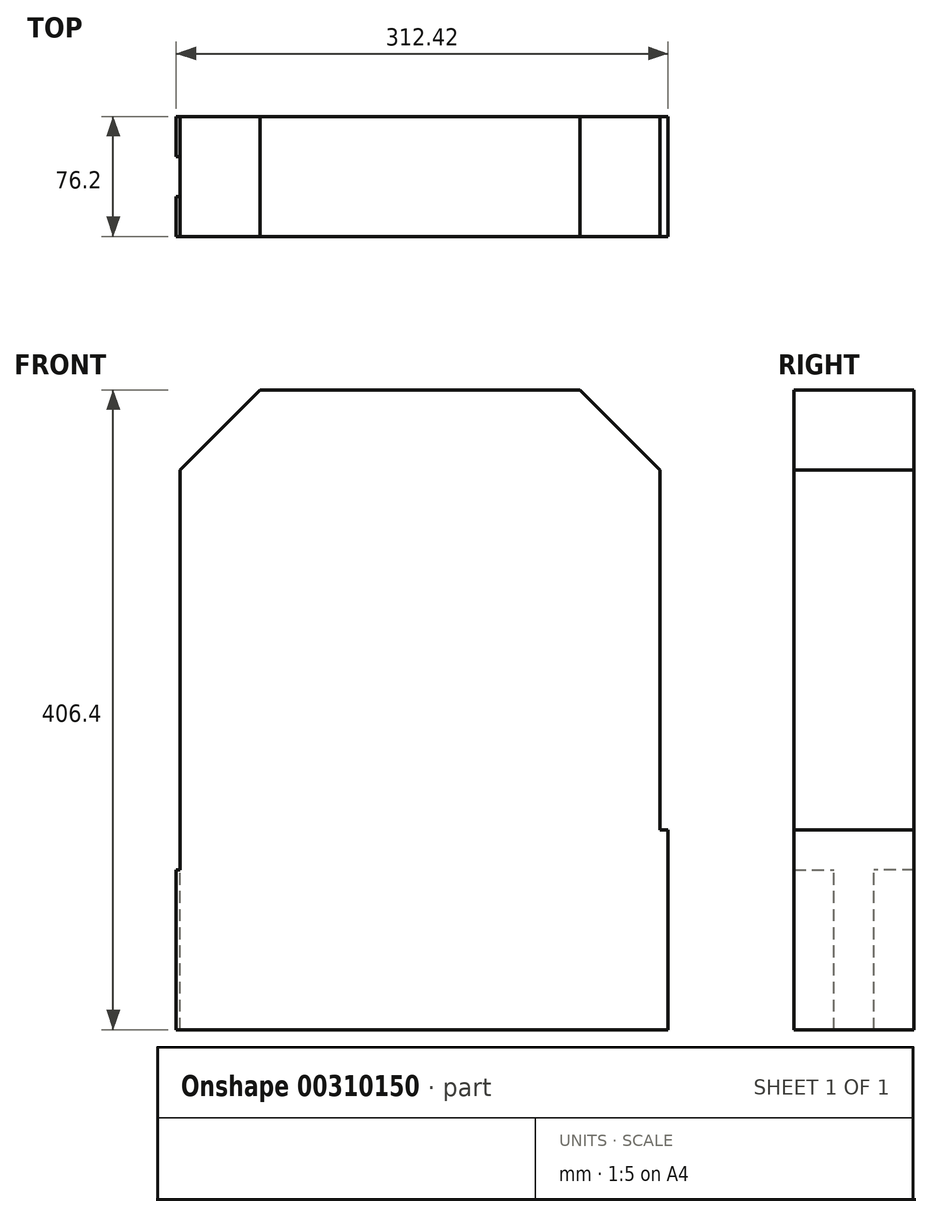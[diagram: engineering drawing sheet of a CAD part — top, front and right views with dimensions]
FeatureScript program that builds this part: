
annotation { "Feature Type Name" : "Feature", "Feature Type Description" : "" }
export const myFeature = defineFeature(function(context is Context, id is Id, definition is map)
    precondition{}
    {
        {
            var Q0;
            Q0=qCreatedBy(makeId("Front.planeOp"),FACE);
            var sketch = newSketch(context, id + "F0", { "sketchPlane" : qUnion([Q0])});
            skLineSegment(sketch, "E0.bottom", {"start": v(-152.4, 203.2) * mm, "end": v(152.4, 203.2) * mm});
            skLineSegment(sketch, "E0.top", {"start": v(-152.4, -203.2) * mm, "end": v(152.4, -203.2) * mm});
            skLineSegment(sketch, "E0.left", {"start": v(-152.4, 203.2) * mm, "end": v(-152.4, -203.2) * mm});
            skLineSegment(sketch, "E0.right", {"start": v(152.4, 203.2) * mm, "end": v(152.4, -203.2) * mm});
            skSolve(sketch);
        }
        {
            var Q0;
            Q0=makeQuery(id+"F0.imprint","IMPRINT",FACE,{"disambiguationData":[TD([[makeQuery(id+"F0.imprint","IMPRINT",EDGE,{"derivedFrom":sQuery(id+"F0.wireOp",EDGE,"E0.bottom")}),-1.0]])]});
            extrude(context, id + "F1", {"entities" : qUnion([Q0]), "depth" : 76.2 * mm});
        }
        {
            var Q0;
            Q0=makeQuery(id+"F1.opExtrude","SWEPT_EDGE",EDGE,{"disambiguationData":[OSD([sQuery(id+"F0.wireOp",EDGE,"E0.bottom"),sQuery(id+"F0.wireOp",EDGE,"E0.left")])]});
            var Q1;
            Q1=makeQuery(id+"F1.opExtrude","SWEPT_EDGE",EDGE,{"disambiguationData":[OSD([sQuery(id+"F0.wireOp",EDGE,"E0.bottom"),sQuery(id+"F0.wireOp",EDGE,"E0.right")])]});
            chamfer(context, id + "F2", {"entities" : qUnion([Q0, Q1]), "width" : 50.8 * mm, "tangentPropagation" : true});
        }
        {
            var Q0;
            Q0=makeQuery(id+"F1.opExtrude","SWEPT_FACE",FACE,{"disambiguationData":[OSD([sQuery(id+"F0.wireOp",EDGE,"E0.left")])]});
            var sketch = newSketch(context, id + "F3", { "sketchPlane" : qUnion([Q0])});
            skLineSegment(sketch, "E1.bottom", {"start": v(0, -203.2) * mm, "end": v(25.4, -203.2) * mm});
            skLineSegment(sketch, "E1.top", {"start": v(0, -101.6) * mm, "end": v(25.4, -101.6) * mm});
            skLineSegment(sketch, "E1.left", {"start": v(0, -203.2) * mm, "end": v(0, -101.6) * mm});
            skLineSegment(sketch, "E1.right", {"start": v(25.4, -203.2) * mm, "end": v(25.4, -101.6) * mm});
            skLineSegment(sketch, "E2.bottom", {"start": v(76.2, -203.2) * mm, "end": v(50.8, -203.2) * mm});
            skLineSegment(sketch, "E2.top", {"start": v(76.2, -101.6) * mm, "end": v(50.8, -101.6) * mm});
            skLineSegment(sketch, "E2.left", {"start": v(76.2, -203.2) * mm, "end": v(76.2, -101.6) * mm});
            skLineSegment(sketch, "E2.right", {"start": v(50.8, -203.2) * mm, "end": v(50.8, -101.6) * mm});
            skSolve(sketch);
        }
        {
            var Q0;
            Q0=makeQuery(id+"F3.imprint","IMPRINT",FACE,{"disambiguationData":[TD([[makeQuery(id+"F3.imprint","IMPRINT",EDGE,{"derivedFrom":sQuery(id+"F3.wireOp",EDGE,"E1.bottom")}),-1.0]])]});
            var Q1;
            Q1=makeQuery(id+"F3.imprint","IMPRINT",FACE,{"disambiguationData":[TD([[makeQuery(id+"F3.imprint","IMPRINT",EDGE,{"derivedFrom":sQuery(id+"F3.wireOp",EDGE,"E2.bottom")}),-1.0]])]});
            extrude(context, id + "F4", {"entities" : qUnion([Q0, Q1]), "operationType" : NewBodyOperationType.ADD, "depth" : 2.54 * mm});
        }
        {
            var Q0;
            Q0=makeQuery(id+"F1.opExtrude","SWEPT_FACE",FACE,{"disambiguationData":[OSD([sQuery(id+"F0.wireOp",EDGE,"E0.right")])]});
            var sketch = newSketch(context, id + "F5", { "sketchPlane" : qUnion([Q0])});
            skLineSegment(sketch, "E3.bottom", {"start": v(-76.2, -203.2) * mm, "end": v(0, -203.2) * mm});
            skLineSegment(sketch, "E3.top", {"start": v(-76.2, -76.2) * mm, "end": v(0, -76.2) * mm});
            skLineSegment(sketch, "E3.left", {"start": v(-76.2, -203.2) * mm, "end": v(-76.2, -76.2) * mm});
            skLineSegment(sketch, "E3.right", {"start": v(0, -203.2) * mm, "end": v(0, -76.2) * mm});
            skLineSegment(sketch, "E4", {"start": v(-76.2, -76.2) * mm, "end": v(0, 152.4) * mm});
            skLineSegment(sketch, "E5", {"start": v(0, 152.4) * mm, "end": v(-76.2, 152.4) * mm});
            skLineSegment(sketch, "E6", {"start": v(-76.2, 152.4) * mm, "end": v(0, -76.2) * mm});
            skLineSegment(sketch, "E7", {"start": v(0, 38.1) * mm, "end": v(-76.2, 38.1) * mm});
            skPoint(sketch, "E7.startSnap0", {"position": v(-38.1, 38.1) * mm});
            skLineSegment(sketch, "E8", {"start": v(-76.2, 38.1) * mm, "end": v(-57.15, 95.25) * mm});
            skLineSegment(sketch, "E9", {"start": v(-57.15, 95.25) * mm, "end": v(-19.05, 95.25) * mm});
            skLineSegment(sketch, "E10", {"start": v(-19.05, 95.25) * mm, "end": v(0, 38.1) * mm});
            skLineSegment(sketch, "E11", {"start": v(-76.2, 38.1) * mm, "end": v(-57.15, -19.05) * mm});
            skLineSegment(sketch, "E12", {"start": v(-57.15, -19.05) * mm, "end": v(-19.05, -19.05) * mm});
            skLineSegment(sketch, "E13", {"start": v(-19.05, -19.05) * mm, "end": v(0, 38.1) * mm});
            skSolve(sketch);
        }
        {
            var Q0;
            Q0=makeQuery(id+"F5.imprint","IMPRINT",FACE,{"disambiguationData":[TD([[makeQuery(id+"F5.imprint","IMPRINT",EDGE,{"derivedFrom":sQuery(id+"F5.wireOp",EDGE,"E3.bottom")}),1.0]])]});
            extrude(context, id + "F6", {"entities" : qUnion([Q0]), "operationType" : NewBodyOperationType.ADD, "depth" : 5.08 * mm});
        }
    });
